# Revit family: ALUTECH_W62_Double_Int.High_bottom_frame_rail_leaf
name_source: partatom
category: Doors
units: mm (PartAtom-declared; Revit-internal decimal feet)

## family parameters
Always vertical = Yes
Classification Number = 23.30.10.00
Cut with Voids When Loaded = No
Host = Wall
Room Calculation Point = No
Shared = No

## types (1)
- 2100x1800
    Air permeability = Class 2
    Analytic Construction = <Нет>
    COBIe Type Category = Doors
    Construction Type = Door.Interior opening.Double opening
    Date of publishing = 2017-02-08
    Design country = Belarus
    Door position in wall = 55 mm  [stored 0.180446 ft]
    Edition number = 1.0
    Facade insert unit = yes
    Function = Interior
    Gap to shell construction = 10 mm  [stored 0.0328084 ft]
    Handle height = 1000 mm  [stored 3.28084 ft]
    Height = 2100 mm
    IFC Classification = Door
    Manufacturer country = Belarus
    Manufacturer name = AluminiumTechno LLC
    Material = Aluminium
    NBS Reference Code = 25-50-20/125
    NBS Reference Description = Frame and door leaf system
    Nominal height = 0
    Nominal width = 0
    Opening type = Inward-opening. Flush-fixed
    Product family = Aluminium door (ALT.W62)
    Product group = Windows and doors
    Rough Height = 2110 mm  [stored 6.92257 ft]
    Rough Width = 1820 mm  [stored 5.97113 ft]
    Sound insulation = -
    Thermal insulation = Uf to 2,83 W/(m2K)
    UNSPSC Code = 30171505
    Uniclass 2.0 Code = SS-25-30-20-30
    Uniclass 2.0 Description = Frame and door leaf systems
    Wall Closure = By host
    Watertightness = Class 2A
    Weight Net (Kg) = 0
    Width = 1800 mm  [stored 5.90551 ft]
    Wind load resistance = Class C4

note: [stored X ft] marks values corroborated as IEEE doubles in the binary element streams (Revit-internal decimal feet)
